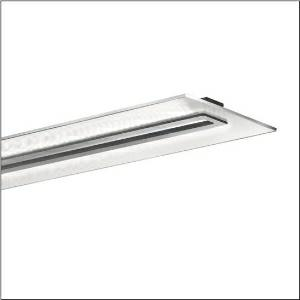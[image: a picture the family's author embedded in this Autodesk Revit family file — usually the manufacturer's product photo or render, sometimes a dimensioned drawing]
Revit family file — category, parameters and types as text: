
# Revit family: vega_r__11_5mn238dlc_e876
name_source: partatom
category: Lighting Fixtures
units: mm (PartAtom-declared; Revit-internal decimal feet)

## family parameters
Cut with Voids When Loaded = No
Host = Face
Light Source = No
Part Type = Normal
Room Calculation Point = No
Round Connector Dimension = Use Diameter
Shared = No

## types (1)
- --- (1 x LED 4000K / CRI = 80 (unbekannt), 4300 lm, 4000K)
    Apparent Load = 31 VA
    CIE Flux Codes = 61 86 97 62 100
    Color Rendering = 80
    Color Temperature = 4000K
    Default Elevation = 1800 mm
    Description = Vega® 11, office luminaire, primary light control with prismatic reflector, of PMMA, transparent prismatic structure, CAT 2 (L<= 1500cd/m²), light emission: direct/indirect distribution, primary light characteristic: symmetric, installation type: suspended mounting, surface-mounted, LED, rated luminous flux: 4.300lm, luminous efficacy: 139lm/W, light colour: 840, colour temperature: 4000K, control gear: DALI, with terminal, 3+2-pole, max. 2.5mm², mains connection: 230V, AC, 50Hz, connection cable inclusive, cable length: 1,5m, rated input power: 31W, luminaire housing, rectangular, rounded, of aluminium section, anodised, metallic grey (RAL 9006), length: 1.250mm, width: 350mm, height: 43mm, luminaire housing, lower part, of aluminium section, anodised, metallic grey (RAL 9006), of PC, grey, protection rating (complete): IP20, insulation class (complete): insulation class I (protective earthing), certification: CE, standard: EN 50419, packaging unit: 1 piece
    Height = 40 mm  [stored 0.131234 ft]
    Lamp = 1 x LED 4000K / CRI >= 80 (unbekannt)
    Lamp Light Flux = 4300 lm
    Lamp count = 1
    Length = 1250 mm
    Luminous efficacy = 139 lm/W
    Manufacturer = Siteco
    ModVariant = No
    Model = 5MN238DLC
    Mounting Place = Ceiling
    Mounting Type = Pendant
    Number of Poles = 1
    OnlyDefault = Yes
    Power Factor = 1
    Product Name = Vega® 11
    Product group = office luminaire | ceiling pendant
    ProductGroupID = 903
    Protection Class = Protection class I
    Protection Degree = IP 20
    RLX_Detail_Level = 1
    RLX_Emergency_Light_Flux = 0 lm
    RLX_Emergency_Type = 0
    RLX_Emergency_Type_DB = No
    RlxData = <blob elided: 62717 chars, md5=635661ae>
    Socket = socket
    Standby Power = 0 W
    System Light Flux = 4300 lm
    System Power = 31 W
    Type Comments = factory setting: luminous flux: 100 % | dim-lin: 254 | 231 mA
    Type Image = l_1004807.jpg
    URL = http://relux.com
    VarID = @adj_220761
    Voltage = 0 V
    Weight = 0.00 kg
    Width = 350 mm

note: [stored X ft] marks values corroborated as IEEE doubles in the binary element streams (Revit-internal decimal feet)

## geometry (parser evidence)
native form markers: Blend x4, Sweep x11
no freeform markers — native parametric forms only
